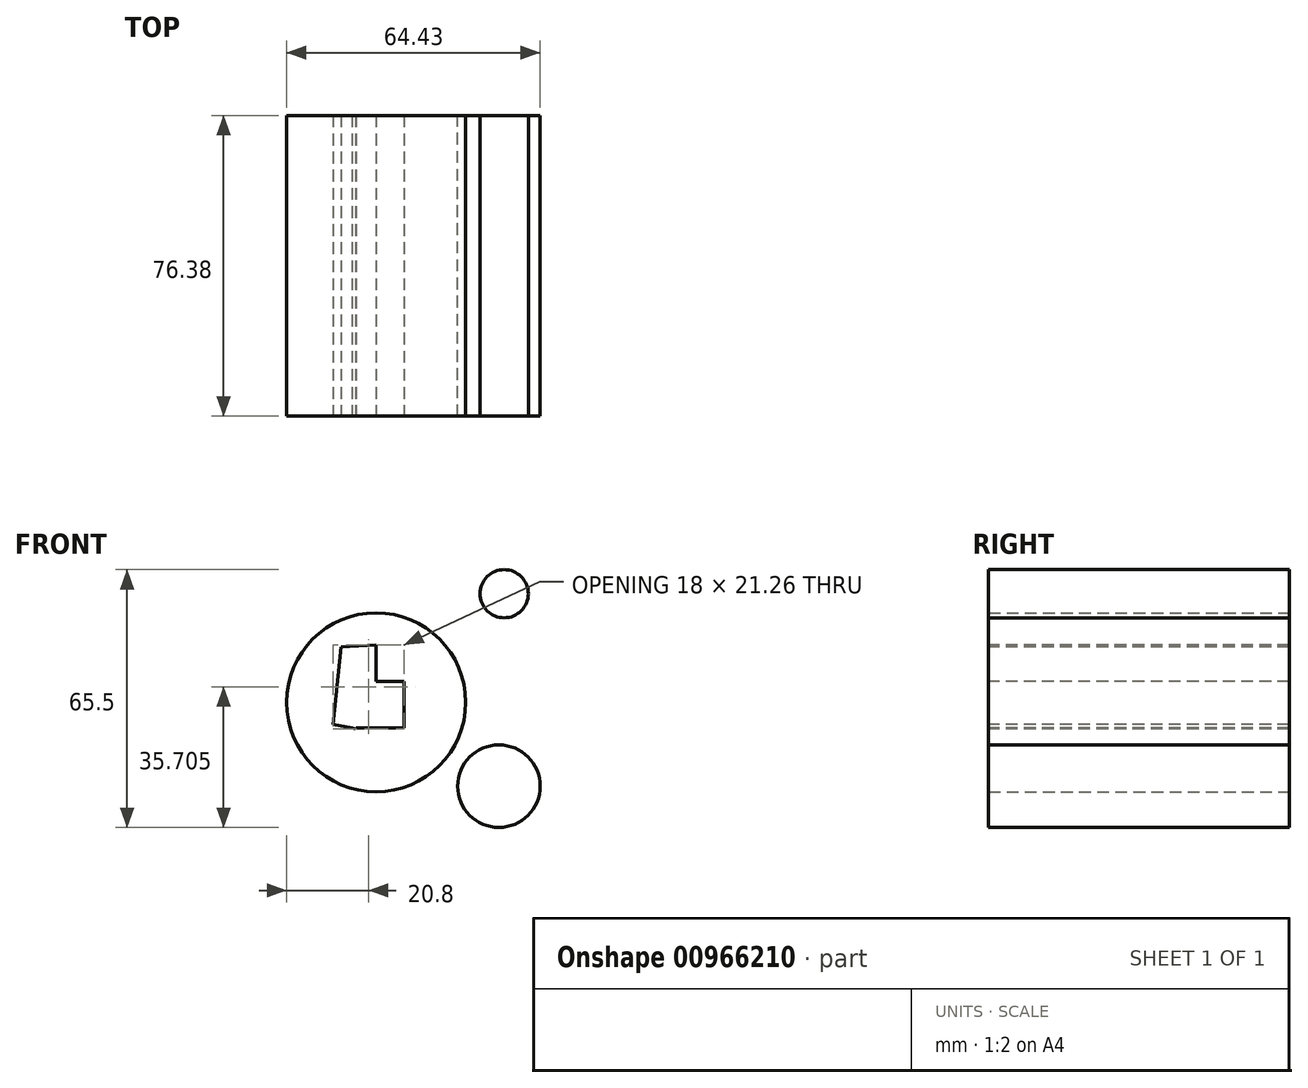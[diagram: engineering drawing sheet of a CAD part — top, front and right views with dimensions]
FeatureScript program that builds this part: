
annotation { "Feature Type Name" : "Feature", "Feature Type Description" : "" }
export const myFeature = defineFeature(function(context is Context, id is Id, definition is map)
    precondition{}
    {
        {
            var Q0;
            Q0=qCreatedBy(makeId("Front.planeOp"),FACE);
            var sketch = newSketch(context, id + "F0", { "sketchPlane" : qUnion([Q0])});
            skCircle(sketch, "E0", {"center": v(32.55, 27.6) * mm, "radius": 6.12 * mm});
            skCircle(sketch, "E1", {"center": v(0, 0) * mm, "radius": 22.75 * mm});
            skCircle(sketch, "E2", {"center": v(31.2, -21.3) * mm, "radius": 10.49 * mm});
            skSolve(sketch);
        }
        {
            var Q0;
            Q0 = qSketchRegion(id + "F0", true);
            extrude(context, id + "F1", {"entities" : qUnion([Q0]), "depth" : 76.38 * mm, "offsetDistance" : 25.4 * mm});
        }
        {
            var Q0;
            Q0=makeQuery(id+"F1.opExtrude","CAP_FACE",FACE,{"disambiguationData":[OSD([sQuery(id+"F0.wireOp",EDGE,"E1")])],"isStart":false});
            var sketch = newSketch(context, id + "F2", { "sketchPlane" : qUnion([Q0])});
            skLineSegment(sketch, "E3", {"start": v(-5.08, -6.46) * mm, "end": v(7.05, -6.46) * mm});
            skLineSegment(sketch, "E4", {"start": v(7.05, -6.46) * mm, "end": v(7.05, 5.25) * mm});
            skLineSegment(sketch, "E5", {"start": v(7.05, 5.25) * mm, "end": v(0, 5.25) * mm});
            skLineSegment(sketch, "E6", {"start": v(0, 5.25) * mm, "end": v(0, 14.55) * mm});
            skLineSegment(sketch, "E7", {"start": v(0, 14.55) * mm, "end": v(-8.85, 14.1) * mm});
            skLineSegment(sketch, "E8", {"start": v(-8.85, 14.1) * mm, "end": v(-10.95, -5.55) * mm});
            skLineSegment(sketch, "E9", {"start": v(-10.95, -5.55) * mm, "end": v(-6.15, -6.45) * mm});
            skLineSegment(sketch, "E10", {"start": v(-6.15, -6.45) * mm, "end": v(-5.18, -6.7) * mm});
            skLineSegment(sketch, "E11", {"start": v(-5.18, -6.7) * mm, "end": v(-5.08, -6.46) * mm});
            skSolve(sketch);
        }
        {
            var Q0;
            Q0 = qSketchRegion(id + "F2", true);
            extrude(context, id + "F3", {"entities" : qUnion([Q0]), "operationType" : NewBodyOperationType.REMOVE, "endBound" : BoundingType.THROUGH_ALL, "oppositeDirection" : true, "depth" : 25.4 * mm, "offsetDistance" : 25.4 * mm});
        }
    });
